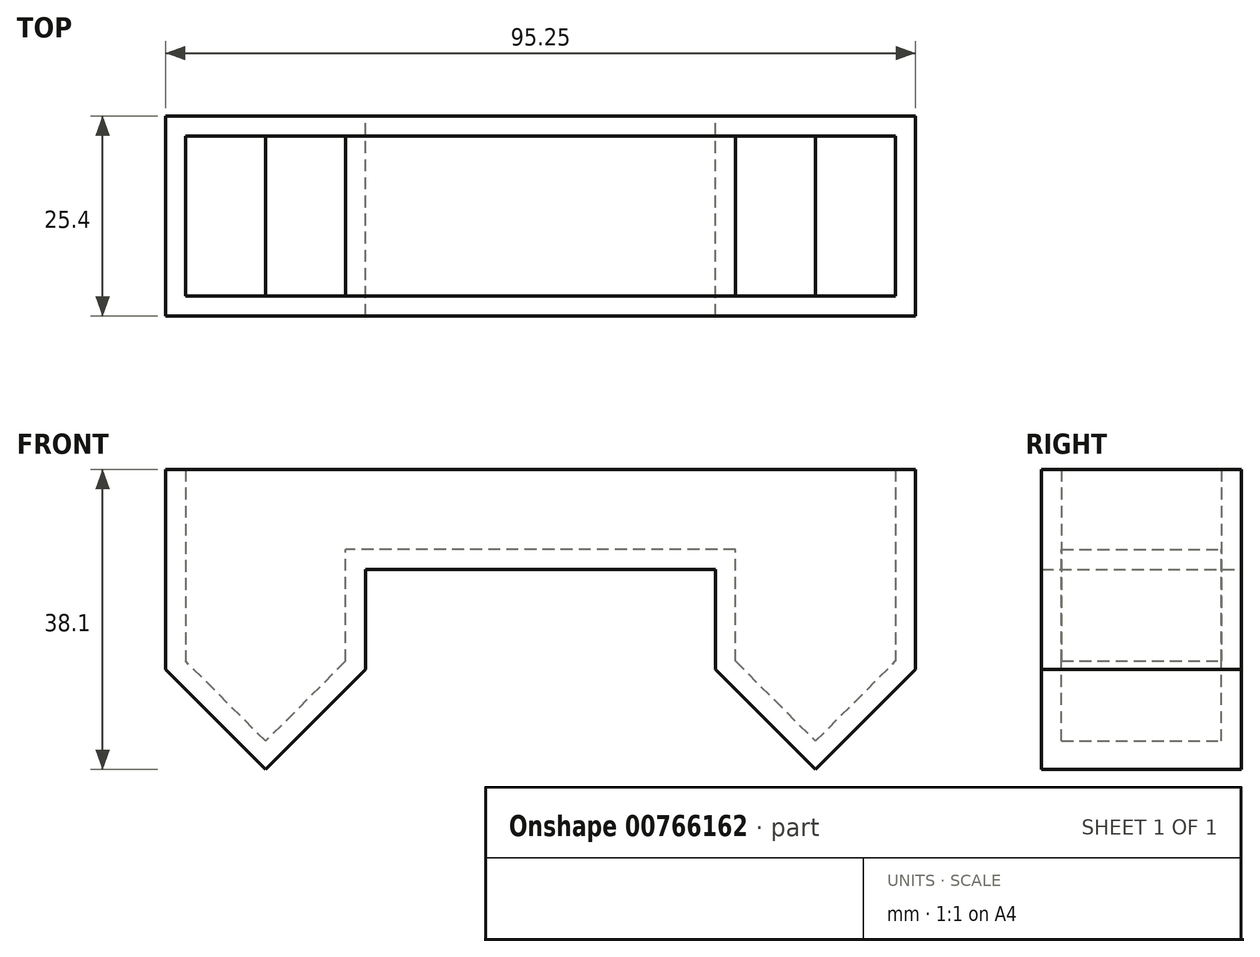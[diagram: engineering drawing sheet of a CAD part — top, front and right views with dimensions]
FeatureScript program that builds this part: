
annotation { "Feature Type Name" : "Feature", "Feature Type Description" : "" }
export const myFeature = defineFeature(function(context is Context, id is Id, definition is map)
    precondition{}
    {
        {
            var Q0;
            Q0=qCreatedBy(makeId("Front.planeOp"),FACE);
            var sketch = newSketch(context, id + "F0", { "sketchPlane" : qUnion([Q0])});
            skLineSegment(sketch, "E0", {"start": v(-44.75, 48.15) * mm, "end": v(2.87, 48.15) * mm});
            skLineSegment(sketch, "E1", {"start": v(2.87, 48.15) * mm, "end": v(2.87, 22.75) * mm});
            skLineSegment(sketch, "E2", {"start": v(-9.83, 10.05) * mm, "end": v(2.87, 22.75) * mm});
            skLineSegment(sketch, "E3", {"start": v(-22.53, 22.75) * mm, "end": v(-9.83, 10.05) * mm});
            skLineSegment(sketch, "E4", {"start": v(-44.75, 48.15) * mm, "end": v(-44.75, 35.45) * mm});
            skLineSegment(sketch, "E5", {"start": v(-22.53, 22.75) * mm, "end": v(-22.53, 35.45) * mm});
            skLineSegment(sketch, "E6", {"start": v(-22.53, 35.45) * mm, "end": v(-44.75, 35.45) * mm});
            skPoint(sketch, "E7.orphan", {"position": v(-44.75, 22.75) * mm});
            skPoint(sketch, "E8.orphan", {"position": v(-92.38, 48.15) * mm});
            skLineSegment(sketch, "E9.MirrorCS", {"start": v(-44.75, 48.15) * mm, "end": v(-92.38, 48.15) * mm});
            skLineSegment(sketch, "E10.MirrorCS", {"start": v(-79.68, 10.05) * mm, "end": v(-92.38, 22.75) * mm});
            skLineSegment(sketch, "E11.MirrorCS", {"start": v(-66.98, 35.45) * mm, "end": v(-44.75, 35.45) * mm});
            skLineSegment(sketch, "E12.MirrorCS", {"start": v(-66.98, 22.75) * mm, "end": v(-66.98, 35.45) * mm});
            skLineSegment(sketch, "E13.MirrorCS", {"start": v(-92.38, 48.15) * mm, "end": v(-92.38, 22.75) * mm});
            skLineSegment(sketch, "E14.MirrorCS", {"start": v(-66.98, 22.75) * mm, "end": v(-79.68, 10.05) * mm});
            skSolve(sketch);
        }
        {
            var Q0;
            Q0=makeQuery(id+"F0.imprint","IMPRINT",FACE,{"disambiguationData":[TD([[makeQuery(id+"F0.imprint","IMPRINT",EDGE,{"derivedFrom":sQuery(id+"F0.wireOp",EDGE,"E0")}),-1.0]])]});
            var Q1;
            Q1=makeQuery(id+"F0.imprint","IMPRINT",FACE,{"disambiguationData":[TD([[makeQuery(id+"F0.imprint","IMPRINT",EDGE,{"derivedFrom":sQuery(id+"F0.wireOp",EDGE,"E4")}),-1.0]])]});
            extrude(context, id + "F1", {"entities" : qUnion([Q0, Q1]), "depth" : 25.4 * mm, "offsetDistance" : 25.4 * mm});
        }
        {
            var Q0;
            Q0=makeQuery(id+"F1.opExtrude","SWEPT_FACE",FACE,{"disambiguationData":[OSD([sQuery(id+"F0.wireOp",EDGE,"E0"),sQuery(id+"F0.wireOp",EDGE,"E9.MirrorCS")])]});
            shell(context, id + "F2", {"entities" : qUnion([Q0]), "thickness" : 2.54 * mm});
        }
    });
